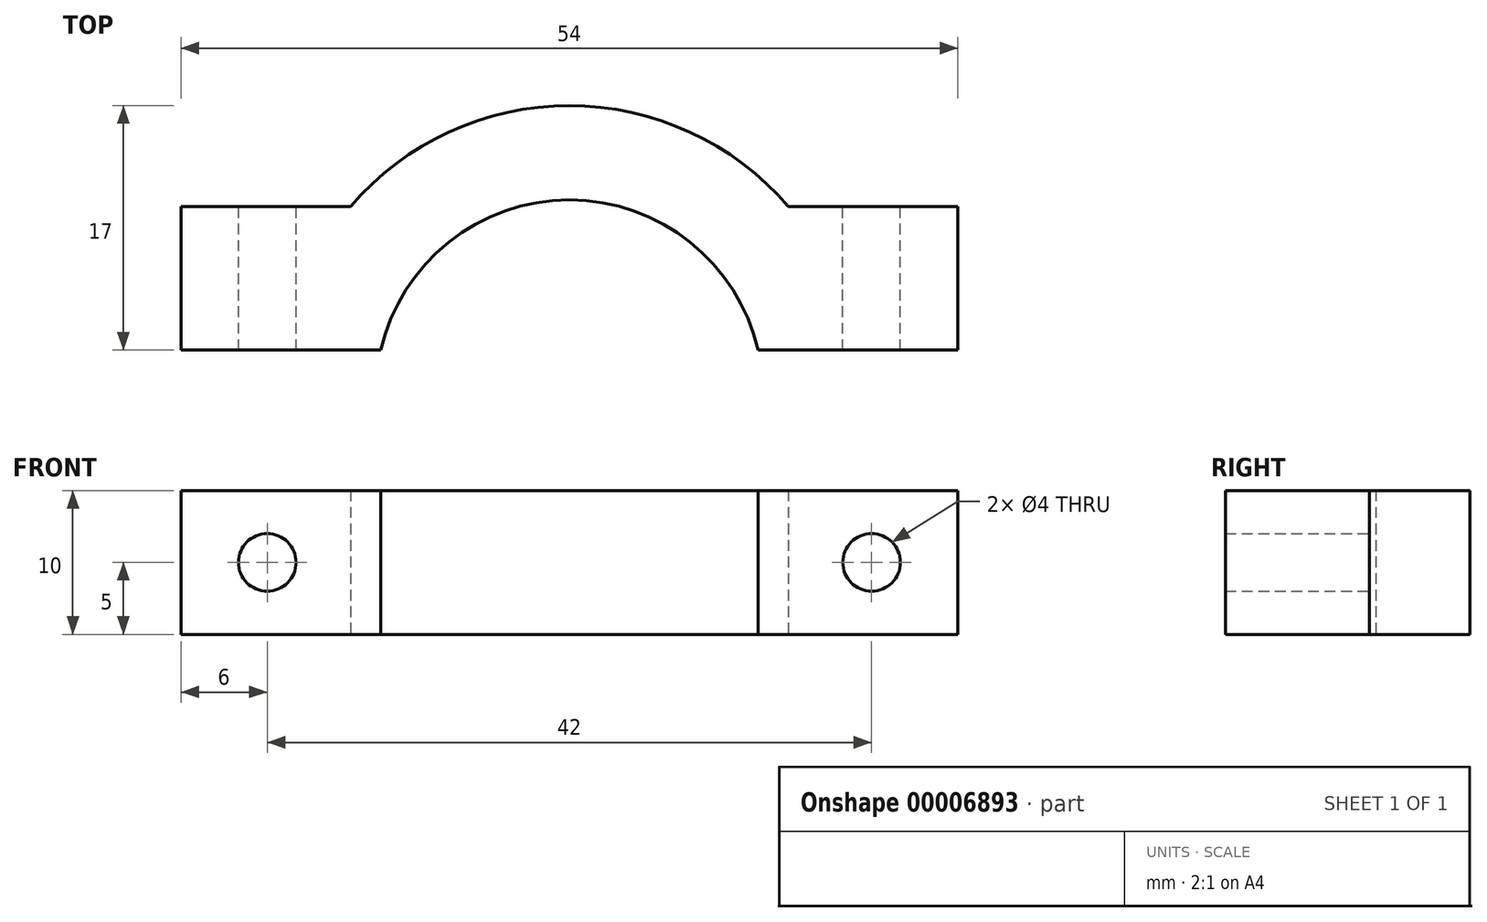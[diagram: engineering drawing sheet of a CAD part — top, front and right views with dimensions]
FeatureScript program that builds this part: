
annotation { "Feature Type Name" : "Feature", "Feature Type Description" : "" }
export const myFeature = defineFeature(function(context is Context, id is Id, definition is map)
    precondition{}
    {
        {
            var Q0;
            Q0=qCreatedBy(makeId("Top.planeOp"),FACE);
            var sketch = newSketch(context, id + "F0", { "sketchPlane" : qUnion([Q0])});
            skArc(sketch, "E0", {"start": v(13.11, 3) * mm, "mid": v(0, 13.45) * mm, "end": v(-13.11, 3) * mm});
            skLineSegment(sketch, "E1", {"start": v(-27, 3) * mm, "end": v(-13.11, 3) * mm});
            skLineSegment(sketch, "E2", {"start": v(27, 3) * mm, "end": v(27, 13) * mm});
            skLineSegment(sketch, "E3", {"start": v(27, 13) * mm, "end": v(15.2, 13) * mm});
            skLineSegment(sketch, "E4", {"start": v(-27, 13) * mm, "end": v(-27, 3) * mm});
            skArc(sketch, "E5", {"start": v(15.2, 13) * mm, "mid": v(0, 20) * mm, "end": v(-15.2, 13) * mm});
            skLineSegment(sketch, "E6.trimOffspring", {"start": v(-15.2, 13) * mm, "end": v(-27, 13) * mm});
            skLineSegment(sketch, "E7.trimOffspring", {"start": v(13.11, 3) * mm, "end": v(27, 3) * mm});
            skSolve(sketch);
        }
        {
            var Q0;
            Q0 = qSketchRegion(id + "F0", true);
            extrude(context, id + "F1", {"entities" : qUnion([Q0]), "depth" : (10) * mm});
        }
        {
            var Q0;
            Q0=makeQuery(id+"F1.opExtrude","SWEPT_FACE",FACE,{"disambiguationData":[OSD([sQuery(id+"F0.wireOp",EDGE,"E3")])]});
            var sketch = newSketch(context, id + "F2", { "sketchPlane" : qUnion([Q0])});
            skCircle(sketch, "E8", {"center": v(-21, 5) * mm, "radius": 2 * mm});
            skLineSegment(sketch, "E9", {"start": v(-27, 5) * mm, "end": v(-13.1, 5) * mm, "construction": true});
            skSolve(sketch);
        }
        {
            var Q0;
            Q0 = qSketchRegion(id + "F2", true);
            extrude(context, id + "F3", {"entities" : qUnion([Q0]), "operationType" : NewBodyOperationType.REMOVE, "endBound" : BoundingType.THROUGH_ALL, "oppositeDirection" : true, "depth" : 25 * mm});
        }
        {
            var Q0;
            Q0=makeQuery(id+"F1.opExtrude","SWEPT_FACE",FACE,{"disambiguationData":[OSD([sQuery(id+"F0.wireOp",EDGE,"E6.trimOffspring")])]});
            var sketch = newSketch(context, id + "F4", { "sketchPlane" : qUnion([Q0])});
            skLineSegment(sketch, "E10", {"start": v(27, 5) * mm, "end": v(15.2, 5) * mm, "construction": true});
            skCircle(sketch, "E11", {"center": v(21, 5) * mm, "radius": 2 * mm});
            skSolve(sketch);
        }
        {
            var Q0;
            Q0 = qSketchRegion(id + "F4", true);
            extrude(context, id + "F5", {"entities" : qUnion([Q0]), "operationType" : NewBodyOperationType.REMOVE, "endBound" : BoundingType.THROUGH_ALL, "oppositeDirection" : true, "depth" : 25 * mm});
        }
    });
